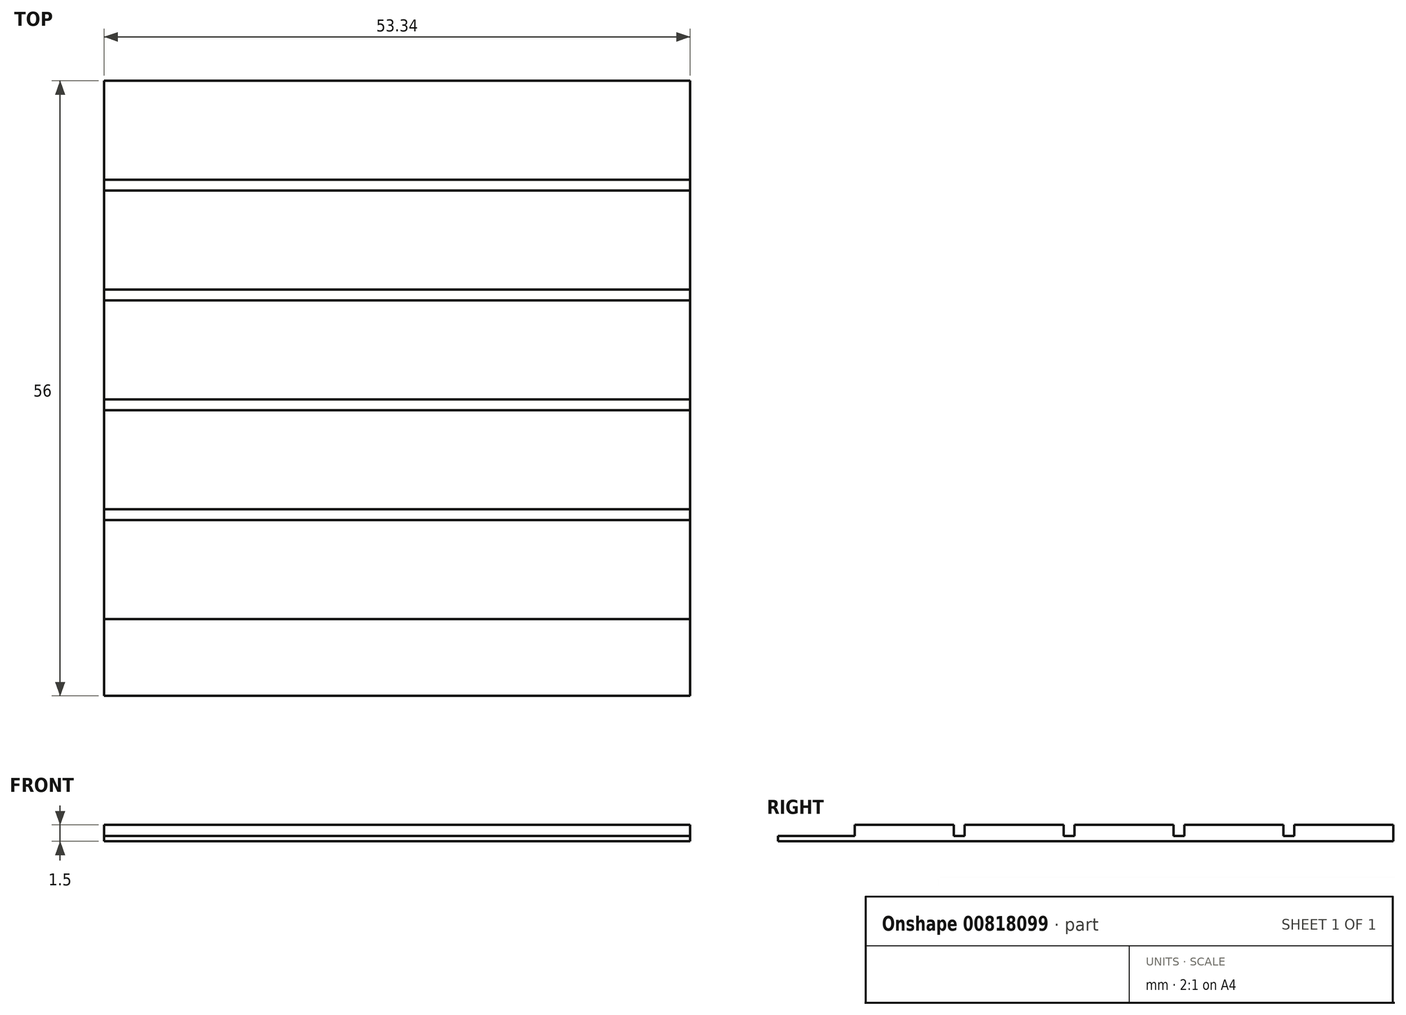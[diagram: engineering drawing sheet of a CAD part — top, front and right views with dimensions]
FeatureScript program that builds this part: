
annotation { "Feature Type Name" : "Feature", "Feature Type Description" : "" }
export const myFeature = defineFeature(function(context is Context, id is Id, definition is map)
    precondition{}
    {
        {
            var Q0;
            Q0=qCreatedBy(makeId("Right.planeOp"),FACE);
            var sketch = newSketch(context, id + "F0", { "sketchPlane" : qUnion([Q0])});
            skLineSegment(sketch, "E0.bottom", {"start": v(-56, -52.69) * mm, "end": v(0, -52.69) * mm});
            skLineSegment(sketch, "E0.top", {"start": v(-56, -53.19) * mm, "end": v(0, -53.19) * mm});
            skLineSegment(sketch, "E0.left", {"start": v(-56, -52.69) * mm, "end": v(-56, -53.19) * mm});
            skLineSegment(sketch, "E0.right", {"start": v(0, -52.69) * mm, "end": v(0, -53.19) * mm});
            skLineSegment(sketch, "E1.bottom", {"start": v(0, -52.69) * mm, "end": v(-9, -52.69) * mm});
            skLineSegment(sketch, "E1.top", {"start": v(0, -51.69) * mm, "end": v(-9, -51.69) * mm});
            skLineSegment(sketch, "E1.left", {"start": v(0, -52.69) * mm, "end": v(0, -51.69) * mm});
            skLineSegment(sketch, "E1.right", {"start": v(-9, -52.69) * mm, "end": v(-9, -51.69) * mm});
            skLineSegment(sketch, "E2.1.0.0", {"start": v(-19, -52.69) * mm, "end": v(-19, -51.69) * mm});
            skLineSegment(sketch, "E2.1.0.1", {"start": v(-10, -52.69) * mm, "end": v(-10, -51.69) * mm});
            skLineSegment(sketch, "E2.1.0.2", {"start": v(-10, -51.69) * mm, "end": v(-19, -51.69) * mm});
            skLineSegment(sketch, "E2.2.0.0", {"start": v(-29, -52.69) * mm, "end": v(-29, -51.69) * mm});
            skLineSegment(sketch, "E2.2.0.1", {"start": v(-20, -52.69) * mm, "end": v(-20, -51.69) * mm});
            skLineSegment(sketch, "E2.2.0.2", {"start": v(-20, -51.69) * mm, "end": v(-29, -51.69) * mm});
            skLineSegment(sketch, "E2.3.0.0", {"start": v(-39, -52.69) * mm, "end": v(-39, -51.69) * mm});
            skLineSegment(sketch, "E2.3.0.1", {"start": v(-30, -52.69) * mm, "end": v(-30, -51.69) * mm});
            skLineSegment(sketch, "E2.3.0.2", {"start": v(-30, -51.69) * mm, "end": v(-39, -51.69) * mm});
            skLineSegment(sketch, "E2.4.0.0", {"start": v(-49, -52.69) * mm, "end": v(-49, -51.69) * mm});
            skLineSegment(sketch, "E2.4.0.1", {"start": v(-40, -52.69) * mm, "end": v(-40, -51.69) * mm});
            skLineSegment(sketch, "E2.4.0.2", {"start": v(-40, -51.69) * mm, "end": v(-49, -51.69) * mm});
            skLineSegment(sketch, "E2.direction1", {"start": v(-9, -52.69) * mm, "end": v(-19, -52.69) * mm, "construction": true});
            skSolve(sketch);
        }
        {
            var Q0;
            Q0 = qSketchRegion(id + "F0", true);
            extrude(context, id + "F1", {"entities" : qUnion([Q0]), "depth" : 53.34 * mm, "offsetDistance" : 25.4 * mm});
        }
    });
